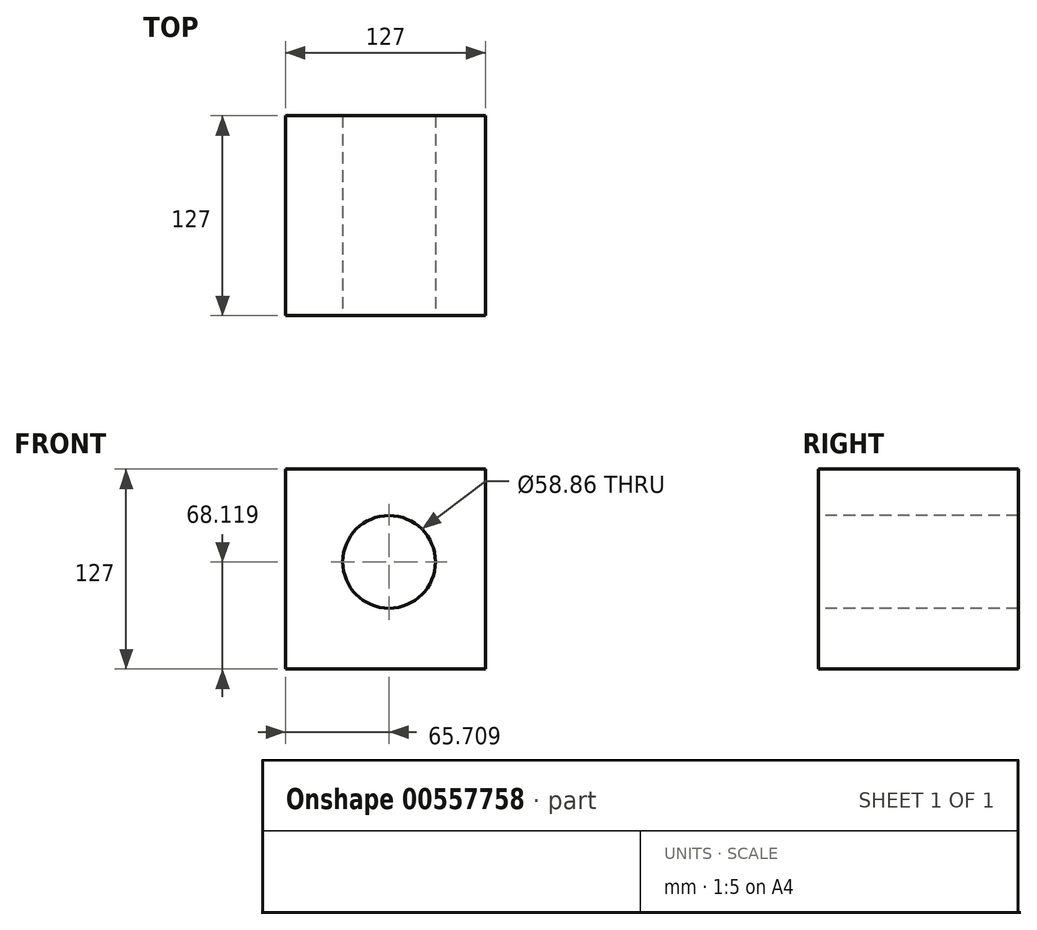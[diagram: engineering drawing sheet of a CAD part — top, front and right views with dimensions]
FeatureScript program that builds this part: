
annotation { "Feature Type Name" : "Feature", "Feature Type Description" : "" }
export const myFeature = defineFeature(function(context is Context, id is Id, definition is map)
    precondition{}
    {
        {
            var Q0;
            Q0=qCreatedBy(makeId("Front.planeOp"),FACE);
            var sketch = newSketch(context, id + "F0", { "sketchPlane" : qUnion([Q0])});
            skLineSegment(sketch, "E0", {"start": v(0, 0) * mm, "end": v(-127, 0) * mm});
            skLineSegment(sketch, "E1", {"start": v(-127, 0) * mm, "end": v(-127, -127) * mm});
            skLineSegment(sketch, "E2", {"start": v(-127, -127) * mm, "end": v(0, -127) * mm});
            skLineSegment(sketch, "E3", {"start": v(0, -127) * mm, "end": v(0, 0) * mm});
            skSolve(sketch);
        }
        {
            var Q0;
            Q0=makeQuery(id+"F0.imprint","IMPRINT",FACE,{"disambiguationData":[TD([[makeQuery(id+"F0.imprint","IMPRINT",EDGE,{"derivedFrom":sQuery(id+"F0.wireOp",EDGE,"E0")}),1.0]])]});
            extrude(context, id + "F1", {"entities" : qUnion([Q0]), "oppositeDirection" : true, "depth" : 127 * mm, "offsetDistance" : 25.4 * mm});
        }
        {
            var Q0;
            Q0=makeQuery(id+"F1.opExtrude","CAP_FACE",FACE,{"disambiguationData":[OSD([sQuery(id+"F0.wireOp",EDGE,"E0"),sQuery(id+"F0.wireOp",EDGE,"E1"),sQuery(id+"F0.wireOp",EDGE,"E2"),sQuery(id+"F0.wireOp",EDGE,"E3")])],"isStart":true});
            var sketch = newSketch(context, id + "F2", { "sketchPlane" : qUnion([Q0])});
            skSolve(sketch);
        }
        {
            var Q0;
            Q0=makeQuery(id+"F2.imprint","IMPRINT",FACE,{"disambiguationData":[TD([[makeQuery(id+"F2.imprint","IMPRINT",EDGE,{"derivedFrom":makeQuery(id+"F1.opExtrude","CAP_EDGE",EDGE,{"disambiguationData":[OSD([sQuery(id+"F0.wireOp",EDGE,"E0")])],"isStart":true})}),1.0]])]});
            var sketch = newSketch(context, id + "F3", { "sketchPlane" : qUnion([Q0])});
            skCircle(sketch, "E4", {"center": v(-61.3, -58.88) * mm, "radius": 29.43 * mm});
            skSolve(sketch);
        }
        {
            var Q0;
            Q0 = qSketchRegion(id + "F3", true);
            extrude(context, id + "F4", {"entities" : qUnion([Q0]), "operationType" : NewBodyOperationType.REMOVE, "oppositeDirection" : true, "depth" : 127 * mm, "offsetDistance" : 25.4 * mm});
        }
    });
